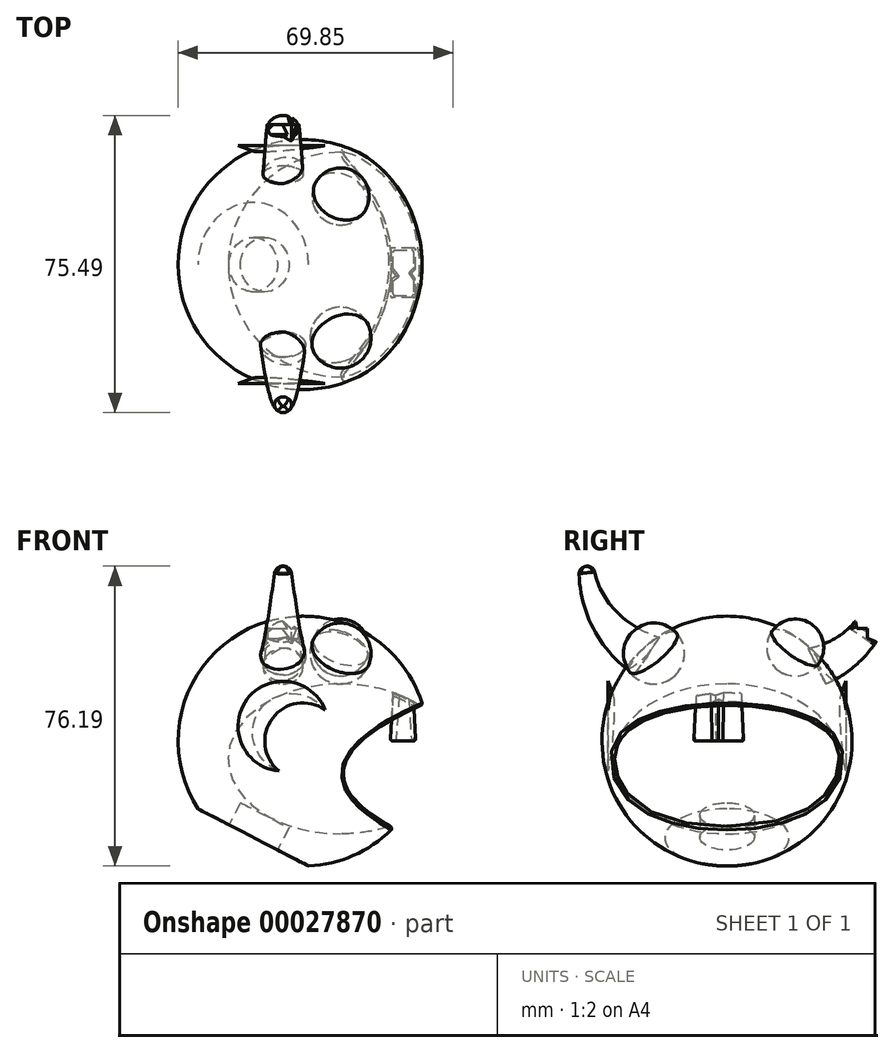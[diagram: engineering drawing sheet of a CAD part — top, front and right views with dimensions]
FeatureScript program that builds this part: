
annotation { "Feature Type Name" : "Feature", "Feature Type Description" : "" }
export const myFeature = defineFeature(function(context is Context, id is Id, definition is map)
    precondition{}
    {
        {
            var Q0;
            Q0=qCreatedBy(makeId("Front.planeOp"),FACE);
            var sketch = newSketch(context, id + "F0", { "sketchPlane" : qUnion([Q0])});
            skArc(sketch, "E0", {"start": v(0, -31.75) * mm, "mid": v(31.75, 0) * mm, "end": v(0, 31.75) * mm});
            skLineSegment(sketch, "E1", {"start": v(0, 31.75) * mm, "end": v(0, -31.75) * mm});
            skSolve(sketch);
        }
        {
            var Q0;
            Q0 = qSketchRegion(id + "F0", true);
            var Q1;
            Q1=sQuery(id+"F0.wireOp",EDGE,"E1");
            revolve(context, id + "F1", {"entities" : qUnion([Q0]), "axis" : qUnion([Q1]), "revolveType" : RevolveType.FULL});
        }
        {
            var Q0;
            Q0=qCreatedBy(makeId("Right.planeOp"),FACE);
            cPlane(context, id + "F2", {"entities" : qUnion([Q0]), "cplaneType" : CPlaneType.OFFSET, "offset" : 9.52 * mm, "width" : 152.4 * mm, "height" : 152.4 * mm});
        }
        {
            var Q0;
            Q0=qCreatedBy(id+"F2.planeOp",FACE);
            var sketch = newSketch(context, id + "F3", { "sketchPlane" : qUnion([Q0])});
            skEllipse(sketch, "E2", {"center": v(0, -4.5) * mm, "majorRadius": 28.58 * mm, "minorRadius": 19.05 * mm, "majorAxis": v(1, 0)});
            skLineSegment(sketch, "E3", {"start": v(0, -23.56) * mm, "end": v(0, 14.54) * mm});
            skSolve(sketch);
        }
        {
            var Q0;
            {var subQ0=sQuery(id+"F3.wireOp",EDGE,"E3");Q0=makeQuery(id+"F3.imprint","IMPRINT",FACE,{"disambiguationData":[TD([[makeQuery(id+"F3.imprint","IMPRINT",EDGE,{"derivedFrom":subQ0}),-1.0]])]});}
            var Q1;
            Q1=sQuery(id+"F3.wireOp",EDGE,"E3");
            revolve(context, id + "F4", {"operationType" : NewBodyOperationType.REMOVE, "entities" : qUnion([Q0]), "axis" : qUnion([Q1]), "revolveType" : RevolveType.FULL});
        }
        {
            var Q0;
            Q0=qCreatedBy(makeId("Top.planeOp"),FACE);
            var sketch = newSketch(context, id + "F5", { "sketchPlane" : qUnion([Q0])});
            skLineSegment(sketch, "E4.bottom", {"start": v(22.23, -8.44) * mm, "end": v(28.58, -8.44) * mm});
            skLineSegment(sketch, "E4.top", {"start": v(22.23, 4.26) * mm, "end": v(28.58, 4.26) * mm});
            skLineSegment(sketch, "E5", {"start": v(28.58, 4.26) * mm, "end": v(28.58, -1.1) * mm});
            skLineSegment(sketch, "E6", {"start": v(28.58, -1.1) * mm, "end": v(27.56, -2.2) * mm});
            skLineSegment(sketch, "E7", {"start": v(27.56, -2.2) * mm, "end": v(28.58, -3.77) * mm});
            skLineSegment(sketch, "E8", {"start": v(28.58, -3.77) * mm, "end": v(28.58, -8.44) * mm});
            skLineSegment(sketch, "E9", {"start": v(22.23, -8.44) * mm, "end": v(22.23, -3.92) * mm});
            skLineSegment(sketch, "E10", {"start": v(22.23, -3.92) * mm, "end": v(23.57, -2.86) * mm});
            skLineSegment(sketch, "E11", {"start": v(23.57, -2.86) * mm, "end": v(22.23, -1.17) * mm});
            skLineSegment(sketch, "E12", {"start": v(22.23, -1.17) * mm, "end": v(22.23, 4.26) * mm});
            skSolve(sketch);
        }
        {
            var Q0;
            Q0 = qSketchRegion(id + "F5", true);
            extrude(context, id + "F6", {"entities" : qUnion([Q0]), "endBound" : BoundingType.UP_TO_NEXT, "depth" : 25.4 * mm, "hasDraft" : true, "draftAngle" : 3 * degree, "draftPullDirection" : true});
        }
        {
            var Q0;
            Q0=makeQuery(id+"F6.opExtrude","CAP_FACE",FACE,{"disambiguationData":[OSD([sQuery(id+"F5.wireOp",EDGE,"E4.bottom"),sQuery(id+"F5.wireOp",EDGE,"E4.top"),sQuery(id+"F5.wireOp",EDGE,"E5"),sQuery(id+"F5.wireOp",EDGE,"E6"),sQuery(id+"F5.wireOp",EDGE,"E7"),sQuery(id+"F5.wireOp",EDGE,"E8"),sQuery(id+"F5.wireOp",EDGE,"E9"),sQuery(id+"F5.wireOp",EDGE,"E10"),sQuery(id+"F5.wireOp",EDGE,"E11"),sQuery(id+"F5.wireOp",EDGE,"E12")])],"isStart":true});
            var Q1;
            Q1=makeQuery(id+"F6.opExtrude","SWEPT_EDGE",EDGE,{"disambiguationData":[OSD([sQuery(id+"F5.wireOp",EDGE,"E4.top"),sQuery(id+"F5.wireOp",EDGE,"E5")])]});
            var Q2;
            Q2=makeQuery(id+"F6.opExtrude","SWEPT_EDGE",EDGE,{"disambiguationData":[OSD([sQuery(id+"F5.wireOp",EDGE,"E4.top"),sQuery(id+"F5.wireOp",EDGE,"E12")])]});
            var Q3;
            Q3=makeQuery(id+"F6.opExtrude","SWEPT_EDGE",EDGE,{"disambiguationData":[OSD([sQuery(id+"F5.wireOp",EDGE,"E4.bottom"),sQuery(id+"F5.wireOp",EDGE,"E8")])]});
            var Q4;
            Q4=makeQuery(id+"F6.opExtrude","SWEPT_EDGE",EDGE,{"disambiguationData":[OSD([sQuery(id+"F5.wireOp",EDGE,"E4.bottom"),sQuery(id+"F5.wireOp",EDGE,"E9")])]});
            fillet(context, id + "F7", {"entities" : qUnion([Q0, Q1, Q2, Q3, Q4]), "radius" : 0.5 * mm, "tangentPropagation" : true, "allowEdgeOverflow" : false});
        }
        {
            var Q0;
            Q0=makeQuery(id+"F4.boolean.opBoolean","INTERSECT",EDGE,{"derivedFrom":[makeQuery(id+"F1.opRevolve","SWEPT_FACE",FACE,{"disambiguationData":[OSD([sQuery(id+"F0.wireOp",EDGE,"E0")])]}),makeQuery(id+"F4.opRevolve","SWEPT_FACE",FACE,{"disambiguationData":[OSD([sQuery(id+"F3.wireOp",EDGE,"E2")])]})]});
            fillet(context, id + "F8", {"entities" : qUnion([Q0]), "radius" : 0.5 * mm, "tangentPropagation" : true, "allowEdgeOverflow" : false});
        }
        {
            var Q0;
            Q0=qCreatedBy(makeId("Front.planeOp"),FACE);
            var sketch = newSketch(context, id + "F9", { "sketchPlane" : qUnion([Q0])});
            skLineSegment(sketch, "E13", {"start": v(21.62, -42.16) * mm, "end": v(-43.49, -8.52) * mm});
            skLineSegment(sketch, "E14", {"start": v(-43.49, -8.52) * mm, "end": v(-43.49, -28.14) * mm});
            skLineSegment(sketch, "E15", {"start": v(-43.49, -28.14) * mm, "end": v(14.32, -57.5) * mm});
            skLineSegment(sketch, "E16", {"start": v(14.32, -57.5) * mm, "end": v(21.62, -42.16) * mm});
            skSolve(sketch);
        }
        {
            var Q0;
            Q0 = qSketchRegion(id + "F9", true);
            extrude(context, id + "F10", {"entities" : qUnion([Q0]), "operationType" : NewBodyOperationType.REMOVE, "endBound" : BoundingType.SYMMETRIC, "oppositeDirection" : true, "depth" : 76.2 * mm});
        }
        {
            var Q0;
            Q0=makeQuery(id+"F10.boolean.opBoolean","COPY",FACE,{"derivedFrom":makeQuery(id+"F10.opExtrude","SWEPT_FACE",FACE,{"disambiguationData":[OSD([sQuery(id+"F9.wireOp",EDGE,"E13")])]})});
            var sketch = newSketch(context, id + "F11", { "sketchPlane" : qUnion([Q0])});
            skCircle(sketch, "E17", {"center": v(0, 0) * mm, "radius": 6.93 * mm});
            skSolve(sketch);
        }
        {
            var Q0;
            Q0 = qSketchRegion(id + "F11", true);
            extrude(context, id + "F12", {"entities" : qUnion([Q0]), "operationType" : NewBodyOperationType.REMOVE, "oppositeDirection" : true, "depth" : 6.35 * mm});
        }
        {
            var Q0;
            Q0=qCreatedBy(id+"F2.planeOp",FACE);
            var sketch = newSketch(context, id + "F13", { "sketchPlane" : qUnion([Q0])});
            skCircle(sketch, "E18", {"center": v(17.34, 23.8) * mm, "radius": 7.23 * mm});
            skCircle(sketch, "E19", {"center": v(-18.57, 22.28) * mm, "radius": 7.73 * mm});
            skLineSegment(sketch, "E20", {"start": v(13.6, 17.6) * mm, "end": v(21.06, 30) * mm});
            skLineSegment(sketch, "E21", {"start": v(-13.58, 16.37) * mm, "end": v(-23.57, 28.19) * mm});
            skSolve(sketch);
        }
        {
            var Q0;
            {var subQ0=sQuery(id+"F13.wireOp",EDGE,"E21");Q0=makeQuery(id+"F13.imprint","IMPRINT",FACE,{"disambiguationData":[TD([[makeQuery(id+"F13.imprint","IMPRINT",EDGE,{"derivedFrom":subQ0}),1.0]])]});}
            var Q1;
            Q1=sQuery(id+"F13.wireOp",EDGE,"E21");
            revolve(context, id + "F14", {"entities" : qUnion([Q0]), "axis" : qUnion([Q1]), "revolveType" : RevolveType.FULL});
        }
        {
            var Q0;
            {var subQ0=sQuery(id+"F13.wireOp",EDGE,"E20");Q0=makeQuery(id+"F13.imprint","IMPRINT",FACE,{"disambiguationData":[TD([[makeQuery(id+"F13.imprint","IMPRINT",EDGE,{"derivedFrom":subQ0}),-1.0]])]});}
            var Q1;
            Q1=sQuery(id+"F13.wireOp",EDGE,"E20");
            revolve(context, id + "F15", {"entities" : qUnion([Q0]), "axis" : qUnion([Q1]), "revolveType" : RevolveType.FULL});
        }
        {
            var Q0;
            Q0=qCreatedBy(makeId("Right.planeOp"),FACE);
            cPlane(context, id + "F16", {"entities" : qUnion([Q0]), "cplaneType" : CPlaneType.OFFSET, "offset" : 5.08 * mm, "oppositeDirection" : true, "width" : 152.4 * mm, "height" : 152.4 * mm});
        }
        {
            var Q0;
            Q0=qCreatedBy(id+"F16.planeOp",FACE);
            var sketch = newSketch(context, id + "F17", { "sketchPlane" : qUnion([Q0])});
            skArc(sketch, "E22", {"start": v(-35.76, 44.45) * mm, "mid": v(-30.28, 31.5) * mm, "end": v(-20.32, 21.59) * mm});
            skArc(sketch, "E23", {"start": v(22.86, 19.05) * mm, "mid": v(33.3, 27.45) * mm, "end": v(39.44, 39.37) * mm});
            skLineSegment(sketch, "E24", {"start": v(-35.76, 44.45) * mm, "end": v(-37.97, 54.94) * mm, "construction": true});
            skLineSegment(sketch, "E25", {"start": v(-20.32, 21.59) * mm, "end": v(-9.36, 14.26) * mm, "construction": true});
            skLineSegment(sketch, "E26", {"start": v(22.86, 19.05) * mm, "end": v(14.5, 14.82) * mm, "construction": true});
            skLineSegment(sketch, "E27", {"start": v(39.44, 39.37) * mm, "end": v(42.17, 49.36) * mm, "construction": true});
            skSolve(sketch);
        }
        {
            var Q0;
            Q0=sQuery(id+"F17.wireOp",EDGE,"E26");
            var Q1;
            Q1=sQuery(id+"F17.wireOp",VERTEX,"E26.start");
            cPlane(context, id + "F18", {"entities" : qUnion([Q0, Q1]), "cplaneType" : CPlaneType.LINE_POINT, "offset" : 152.4 * mm, "width" : 152.4 * mm, "height" : 152.4 * mm});
        }
        {
            var Q0;
            Q0=qCreatedBy(id+"F18.planeOp",FACE);
            var sketch = newSketch(context, id + "F19", { "sketchPlane" : qUnion([Q0])});
            skCircle(sketch, "E28", {"center": v(-5.08, 6.67) * mm, "radius": 5.08 * mm});
            skSolve(sketch);
        }
        {
            var Q0;
            Q0=sQuery(id+"F17.wireOp",EDGE,"E25");
            var Q1;
            Q1=sQuery(id+"F17.wireOp",VERTEX,"E25.start");
            cPlane(context, id + "F20", {"entities" : qUnion([Q0, Q1]), "cplaneType" : CPlaneType.LINE_POINT, "offset" : 152.4 * mm, "width" : 152.4 * mm, "height" : 152.4 * mm});
        }
        {
            var Q0;
            Q0=qCreatedBy(id+"F20.planeOp",FACE);
            var sketch = newSketch(context, id + "F21", { "sketchPlane" : qUnion([Q0])});
            skCircle(sketch, "E29", {"center": v(5.08, 6.65) * mm, "radius": 5.72 * mm});
            skSolve(sketch);
        }
        {
            var Q0;
            Q0=sQuery(id+"F17.wireOp",VERTEX,"E24.start");
            var Q1;
            Q1=sQuery(id+"F17.wireOp",EDGE,"E24");
            cPlane(context, id + "F22", {"entities" : qUnion([Q0, Q1]), "cplaneType" : CPlaneType.LINE_POINT, "offset" : 152.4 * mm, "width" : 152.4 * mm, "height" : 152.4 * mm});
        }
        {
            var Q0;
            Q0=qCreatedBy(id+"F22.planeOp",FACE);
            var sketch = newSketch(context, id + "F23", { "sketchPlane" : qUnion([Q0])});
            skCircle(sketch, "E30", {"center": v(-5.08, -25.86) * mm, "radius": 1.9 * mm});
            skSolve(sketch);
        }
        {
            var Q0;
            Q0=sQuery(id+"F17.wireOp",EDGE,"E27");
            var Q1;
            Q1=sQuery(id+"F17.wireOp",VERTEX,"E27.start");
            cPlane(context, id + "F24", {"entities" : qUnion([Q0, Q1]), "cplaneType" : CPlaneType.LINE_POINT, "offset" : 152.4 * mm, "width" : 152.4 * mm, "height" : 152.4 * mm});
        }
        {
            var Q0;
            Q0=qCreatedBy(id+"F24.planeOp",FACE);
            var sketch = newSketch(context, id + "F25", { "sketchPlane" : qUnion([Q0])});
            skCircle(sketch, "E31", {"center": v(-5.08, 27.67) * mm, "radius": 3.18 * mm});
            skSolve(sketch);
        }
        {
            var Q0;
            Q0=qCreatedBy(id+"F16.planeOp",FACE);
            var sketch = newSketch(context, id + "F26", { "sketchPlane" : qUnion([Q0])});
            skArc(sketch, "E32", {"start": v(-37.63, 44.06) * mm, "mid": v(-33.98, 28.67) * mm, "end": v(-23.5, 16.84) * mm});
            skArc(sketch, "E33", {"start": v(25.15, 14.52) * mm, "mid": v(37.12, 24.15) * mm, "end": v(42.5, 38.53) * mm});
            skSolve(sketch);
        }
        {
            var Q1;
            Q1 = qSketchRegion(id + "F21", true);
            var Q2;
            Q2 = qSketchRegion(id + "F23", true);
            var Q3;
            Q3=sQuery(id+"F26.wireOp",EDGE,"E32");
            loft(context, id + "F27", {"addGuides" : true, "sheetProfilesArray" : [{ "sheetProfileEntities" : qUnion([Q1]) }, { "sheetProfileEntities" : qUnion([Q2]) }], "guidesArray" : [{ "guideEntities" : qUnion([Q3]), "guideDerivativeType" : LoftGuideDerivativeType.DEFAULT, "guideDerivativeMagnitude" : 1 }]});
        }
        {
            var Q1;
            Q1 = qSketchRegion(id + "F25", true);
            var Q2;
            Q2 = qSketchRegion(id + "F19", true);
            var Q3;
            Q3=sQuery(id+"F26.wireOp",EDGE,"E33");
            loft(context, id + "F28", {"addGuides" : true, "sheetProfilesArray" : [{ "sheetProfileEntities" : qUnion([Q1]) }, { "sheetProfileEntities" : qUnion([Q2]) }], "guidesArray" : [{ "guideEntities" : qUnion([Q3]), "guideDerivativeType" : LoftGuideDerivativeType.DEFAULT, "guideDerivativeMagnitude" : 1 }]});
        }
        {
            var Q0;
            Q0=makeQuery(id+"F27.opLoft","MID_CAP_EDGE",EDGE,{"disambiguationData":[OSD([sQuery(id+"F23.wireOp",EDGE,"E30"),sQuery(id+"F26.wireOp",EDGE,"E32")])],"capPos":1.0});
            fillet(context, id + "F29", {"entities" : qUnion([Q0]), "radius" : 1.9 * mm, "tangentPropagation" : true, "allowEdgeOverflow" : false});
        }
        {
            var Q0;
            Q0=qCreatedBy(id+"F16.planeOp",FACE);
            var sketch = newSketch(context, id + "F30", { "sketchPlane" : qUnion([Q0])});
            skLineSegment(sketch, "E34", {"start": v(42.34, 23.48) * mm, "end": v(35.63, 26.15) * mm});
            skLineSegment(sketch, "E35", {"start": v(35.63, 26.15) * mm, "end": v(35.63, 28.6) * mm});
            skLineSegment(sketch, "E36", {"start": v(35.63, 28.6) * mm, "end": v(33.01, 28.6) * mm});
            skLineSegment(sketch, "E37", {"start": v(33.01, 28.6) * mm, "end": v(32.03, 32.6) * mm});
            skLineSegment(sketch, "E38", {"start": v(32.03, 32.6) * mm, "end": v(36.21, 44.61) * mm});
            skLineSegment(sketch, "E39", {"start": v(36.21, 44.61) * mm, "end": v(47.25, 42.03) * mm});
            skLineSegment(sketch, "E40", {"start": v(47.25, 42.03) * mm, "end": v(42.34, 23.48) * mm});
            skSolve(sketch);
        }
        {
            var Q0;
            Q0 = qSketchRegion(id + "F30", true);
            extrude(context, id + "F31", {"entities" : qUnion([Q0]), "operationType" : NewBodyOperationType.REMOVE, "endBound" : BoundingType.SYMMETRIC, "oppositeDirection" : true, "depth" : 25.4 * mm});
        }
        {
            var Q0;
            Q0=qCreatedBy(id+"F20.planeOp",FACE);
            var sketch = newSketch(context, id + "F32", { "sketchPlane" : qUnion([Q0])});
            skLineSegment(sketch, "E41", {"start": v(14.61, 39.44) * mm, "end": v(6.08, 44.55) * mm});
            skLineSegment(sketch, "E42", {"start": v(6.08, 44.55) * mm, "end": v(2.9, 41.06) * mm});
            skLineSegment(sketch, "E43", {"start": v(2.9, 41.06) * mm, "end": v(0, 47.2) * mm});
            skLineSegment(sketch, "E44", {"start": v(0, 47.2) * mm, "end": v(11, 52.42) * mm});
            skLineSegment(sketch, "E45", {"start": v(11, 52.42) * mm, "end": v(14.61, 39.44) * mm});
            skSolve(sketch);
        }
        {
            var Q0;
            Q0 = qSketchRegion(id + "F32", true);
            extrude(context, id + "F33", {"entities" : qUnion([Q0]), "operationType" : NewBodyOperationType.REMOVE, "depth" : 101.6 * mm});
        }
        {
            var Q0;
            Q0=makeQuery(id+"F14.opRevolve","SWEPT_BODY",BODY,{"disambiguationData":[OSD([sQuery(id+"F13.wireOp",EDGE,"E19"),sQuery(id+"F13.wireOp",EDGE,"E21")])]});
            var Q1;
            Q1=makeQuery(id+"F15.opRevolve","SWEPT_BODY",BODY,{"disambiguationData":[OSD([sQuery(id+"F13.wireOp",EDGE,"E18"),sQuery(id+"F13.wireOp",EDGE,"E20")])]});
            var Q2;
            Q2=makeQuery(id+"F27.opLoft","SWEPT_BODY",BODY,{"disambiguationData":[OSD([makeQuery(id+"F21.imprint","IMPRINT",FACE,{"disambiguationData":[TD([[makeQuery(id+"F21.imprint","IMPRINT",EDGE,{"derivedFrom":sQuery(id+"F21.wireOp",EDGE,"E29")}),1.0]])]}),makeQuery(id+"F23.imprint","IMPRINT",FACE,{"disambiguationData":[TD([[makeQuery(id+"F23.imprint","IMPRINT",EDGE,{"derivedFrom":sQuery(id+"F23.wireOp",EDGE,"E30")}),1.0]])]}),sQuery(id+"F26.wireOp",EDGE,"E32")])]});
            var Q3;
            Q3=makeQuery(id+"F28.opLoft","SWEPT_BODY",BODY,{"disambiguationData":[OSD([makeQuery(id+"F19.imprint","IMPRINT",FACE,{"disambiguationData":[TD([[makeQuery(id+"F19.imprint","IMPRINT",EDGE,{"derivedFrom":sQuery(id+"F19.wireOp",EDGE,"E28")}),1.0]])]}),makeQuery(id+"F25.imprint","IMPRINT",FACE,{"disambiguationData":[TD([[makeQuery(id+"F25.imprint","IMPRINT",EDGE,{"derivedFrom":sQuery(id+"F25.wireOp",EDGE,"E31")}),1.0]])]}),sQuery(id+"F26.wireOp",EDGE,"E33")])]});
            var Q4;
            Q4=makeQuery(id+"F1.opRevolve","SWEPT_BODY",BODY,{"disambiguationData":[OSD([sQuery(id+"F0.wireOp",EDGE,"E0"),sQuery(id+"F0.wireOp",EDGE,"E1")])]});
            var Q5;
            Q5=makeQuery(id+"F14.opRevolve","SWEPT_FACE",FACE,{"disambiguationData":[OSD([sQuery(id+"F13.wireOp",EDGE,"E19")])]});
            var Q6;
            Q6=makeQuery(id+"F15.opRevolve","SWEPT_FACE",FACE,{"disambiguationData":[OSD([sQuery(id+"F13.wireOp",EDGE,"E18")])]});
            var Q7;
            Q7=makeQuery(id+"F28.opLoft","SWEPT_FACE",FACE,{"disambiguationData":[OSD([sQuery(id+"F19.wireOp",EDGE,"E28"),sQuery(id+"F25.wireOp",EDGE,"E31"),sQuery(id+"F26.wireOp",EDGE,"E33")])]});
            var Q8;
            Q8=makeQuery(id+"F27.opLoft","SWEPT_FACE",FACE,{"disambiguationData":[OSD([sQuery(id+"F21.wireOp",EDGE,"E29"),sQuery(id+"F23.wireOp",EDGE,"E30"),sQuery(id+"F26.wireOp",EDGE,"E32")])]});
            booleanBodies(context, id + "F34", {"operationType" : BooleanOperationType.SUBTRACTION, "tools" : qUnion([Q0, Q1, Q2, Q3]), "targets" : qUnion([Q4]), "offset" : true, "entitiesToOffset" : qUnion([Q5, Q6, Q7, Q8]), "offsetDistance" : 0.03 * mm, "keepTools" : true});
        }
        {
            var Q0;
            Q0=qCreatedBy(id+"F16.planeOp",FACE);
            var sketch = newSketch(context, id + "F35", { "sketchPlane" : qUnion([Q0])});
            skLineSegment(sketch, "E46", {"start": v(26.07, 3.81) * mm, "end": v(30.23, 3.81) * mm});
            skLineSegment(sketch, "E47", {"start": v(30.23, 3.81) * mm, "end": v(30.23, 15.24) * mm});
            skLineSegment(sketch, "E48", {"start": v(30.23, 15.24) * mm, "end": v(26.07, 3.8) * mm});
            skSolve(sketch);
        }
        {
            var Q0;
            Q0 = qSketchRegion(id + "F35", true);
            var Q1;
            Q1=sQuery(id+"F35.wireOp",EDGE,"E46");
            revolve(context, id + "F36", {"entities" : qUnion([Q0]), "axis" : qUnion([Q1]), "revolveType" : RevolveType.FULL});
        }
        {
            var Q0;
            Q0=makeQuery(id+"F36.opRevolve","SWEPT_BODY",BODY,{"disambiguationData":[OSD([sQuery(id+"F35.wireOp",EDGE,"E46"),sQuery(id+"F35.wireOp",EDGE,"E47"),sQuery(id+"F35.wireOp",EDGE,"E48")])]});
            var Q1;
            Q1=qCreatedBy(makeId("Front.planeOp"),FACE);
            mirror(context, id + "F37", {"operationType" : NewBodyOperationType.ADD, "entities" : qUnion([Q0]), "mirrorPlane" : qUnion([Q1])});
        }
    });
